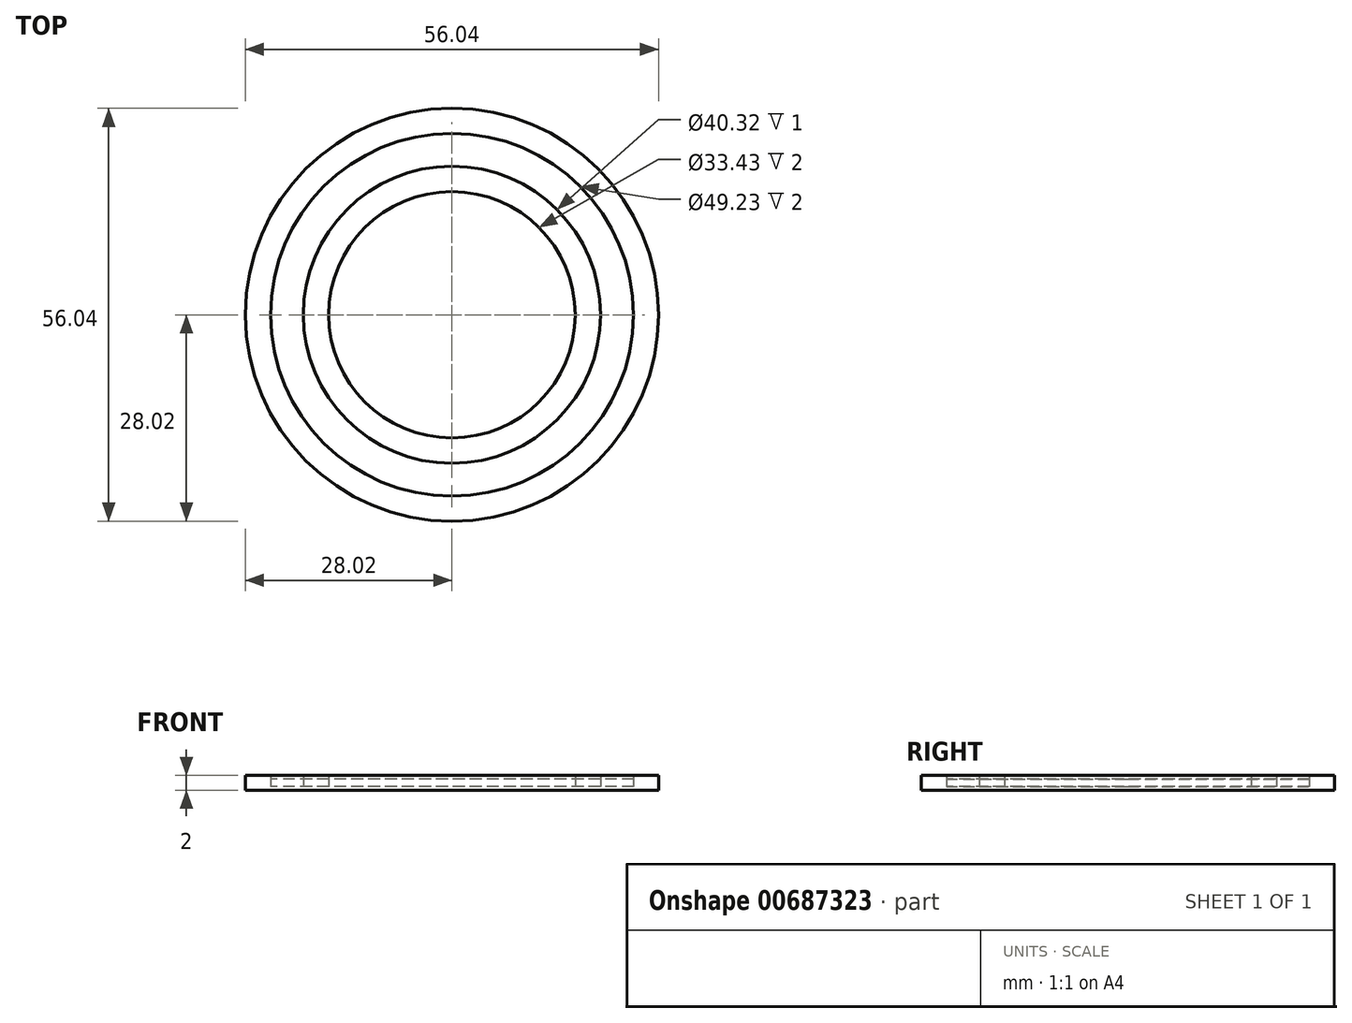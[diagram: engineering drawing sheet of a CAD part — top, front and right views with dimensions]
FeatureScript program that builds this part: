
annotation { "Feature Type Name" : "Feature", "Feature Type Description" : "" }
export const myFeature = defineFeature(function(context is Context, id is Id, definition is map)
    precondition{}
    {
        {
            var Q0;
            Q0=qCreatedBy(makeId("Top.planeOp"),FACE);
            var sketch = newSketch(context, id + "F0", { "sketchPlane" : qUnion([Q0])});
            skCircle(sketch, "E0", {"center": v(0, 0) * mm, "radius": 16.72 * mm});
            skCircle(sketch, "E1", {"center": v(0, 0) * mm, "radius": 20.16 * mm});
            skCircle(sketch, "E2", {"center": v(0, 0) * mm, "radius": 24.61 * mm});
            skCircle(sketch, "E3", {"center": v(0, 0) * mm, "radius": 28.02 * mm});
            skSolve(sketch);
        }
        {
            var Q0;
            Q0=makeQuery(id+"F0.imprint","IMPRINT",FACE,{"disambiguationData":[TD([[makeQuery(id+"F0.imprint","IMPRINT",EDGE,{"derivedFrom":sQuery(id+"F0.wireOp",EDGE,"E2")}),-1.0]])]});
            var Q1;
            Q1=makeQuery(id+"F0.imprint","IMPRINT",FACE,{"disambiguationData":[TD([[makeQuery(id+"F0.imprint","IMPRINT",EDGE,{"derivedFrom":sQuery(id+"F0.wireOp",EDGE,"E0")}),-1.0]])]});
            extrude(context, id + "F1", {"entities" : qUnion([Q0, Q1]), "endBound" : BoundingType.SYMMETRIC, "depth" : 2 * mm, "offsetDistance" : 25 * mm});
        }
        {
            var Q0;
            Q0=makeQuery(id+"F0.imprint","IMPRINT",FACE,{"disambiguationData":[TD([[makeQuery(id+"F0.imprint","IMPRINT",EDGE,{"derivedFrom":sQuery(id+"F0.wireOp",EDGE,"E1")}),-1.0]])]});
            extrude(context, id + "F2", {"entities" : qUnion([Q0]), "endBound" : BoundingType.SYMMETRIC, "depth" : 1 * mm, "offsetDistance" : 25 * mm});
        }
    });
